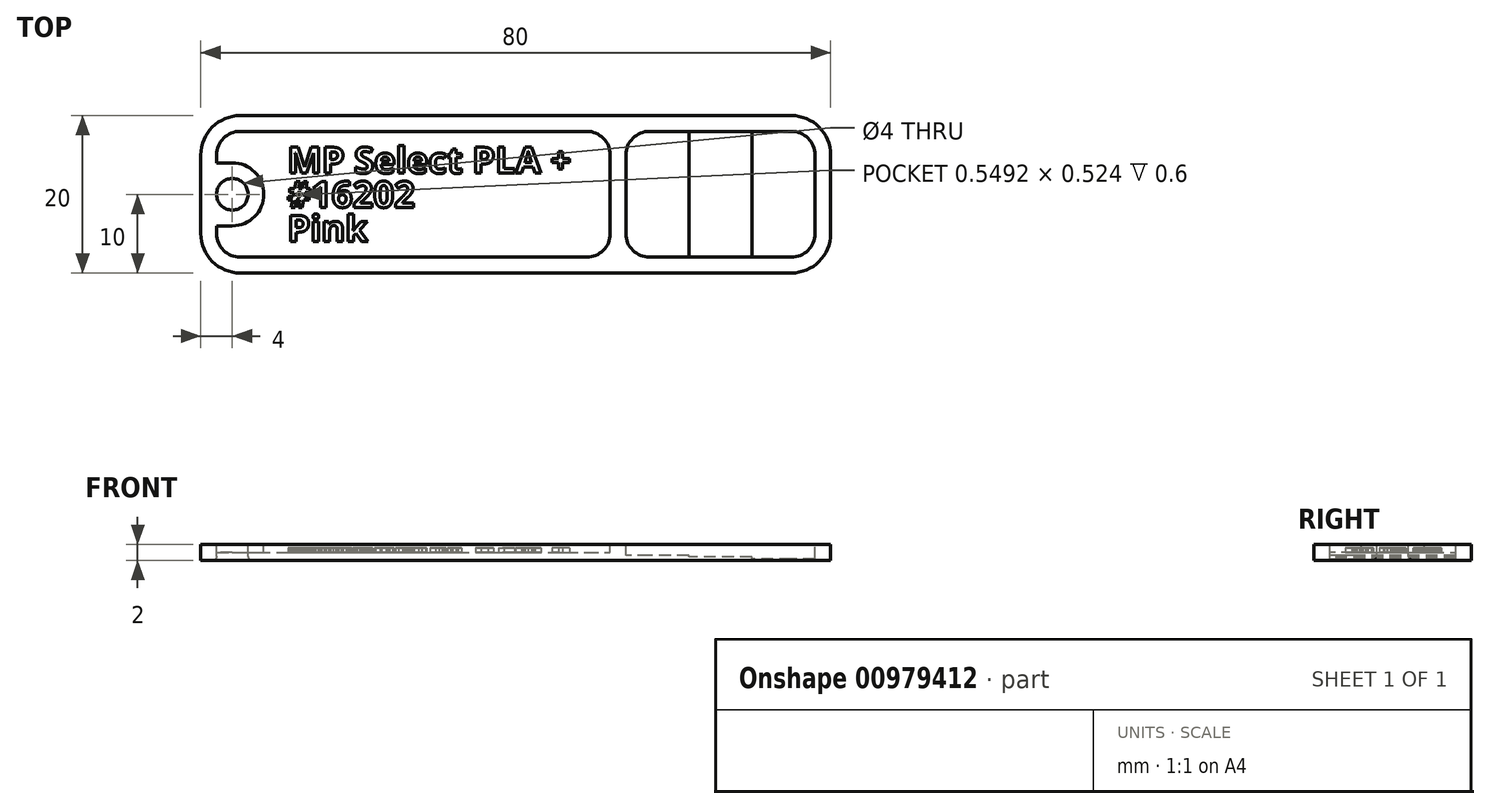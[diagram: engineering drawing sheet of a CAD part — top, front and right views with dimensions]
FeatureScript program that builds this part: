
annotation { "Feature Type Name" : "Feature", "Feature Type Description" : "" }
export const myFeature = defineFeature(function(context is Context, id is Id, definition is map)
    precondition{}
    {
        {
            var Q0;
            Q0=qCreatedBy(makeId("Top.planeOp"),FACE);
            var sketch = newSketch(context, id + "F0", { "sketchPlane" : qUnion([Q0])});
            skLineSegment(sketch, "E0.bottom", {"start": v(35, 10) * mm, "end": v(-35, 10) * mm});
            skLineSegment(sketch, "E0.top", {"start": v(35, -10) * mm, "end": v(-35, -10) * mm});
            skLineSegment(sketch, "E0.left", {"start": v(40, 5) * mm, "end": v(40, -5) * mm});
            skLineSegment(sketch, "E0.right", {"start": v(-40, 5) * mm, "end": v(-40, -5) * mm});
            skPoint(sketch, "E0.middle", {"position": v(0, 0) * mm});
            skPoint(sketch, "E1.visualSharp", {"position": v(-40, 10) * mm});
            skArc(sketch, "E1.filletArc", {"start": v(-35, 10) * mm, "mid": v(-38.54, 8.54) * mm, "end": v(-40, 5) * mm});
            skPoint(sketch, "E2.visualSharp", {"position": v(40, 10) * mm});
            skArc(sketch, "E2.filletArc", {"start": v(40, 5) * mm, "mid": v(38.54, 8.54) * mm, "end": v(35, 10) * mm});
            skPoint(sketch, "E3.visualSharp", {"position": v(40, -10) * mm});
            skArc(sketch, "E3.filletArc", {"start": v(35, -10) * mm, "mid": v(38.54, -8.54) * mm, "end": v(40, -5) * mm});
            skPoint(sketch, "E4.visualSharp", {"position": v(-40, -10) * mm});
            skArc(sketch, "E4.filletArc", {"start": v(-40, -5) * mm, "mid": v(-38.54, -8.54) * mm, "end": v(-35, -10) * mm});
            skSolve(sketch);
        }
        {
            var Q0;
            Q0=qSketchRegion(id+"F0",true);
            extrude(context, id + "F1", {"entities" : qUnion([Q0]), "offsetDistance" : 25 * mm, "depth" : 2 * mm});
        }
        {
            var Q0;
            Q0=makeQuery(id+"F1.opExtrude","CAP_FACE",FACE,{"disambiguationData":[OSD([sQuery(id+"F0.wireOp",EDGE,"E0.bottom"),sQuery(id+"F0.wireOp",EDGE,"E0.top"),sQuery(id+"F0.wireOp",EDGE,"E0.left"),sQuery(id+"F0.wireOp",EDGE,"E0.right"),sQuery(id+"F0.wireOp",EDGE,"E1.filletArc"),sQuery(id+"F0.wireOp",EDGE,"E2.filletArc"),sQuery(id+"F0.wireOp",EDGE,"E3.filletArc"),sQuery(id+"F0.wireOp",EDGE,"E4.filletArc")])],"isStart":false});
            var sketch = newSketch(context, id + "F2", { "sketchPlane" : qUnion([Q0])});
            skLineSegment(sketch, "E5.0", {"start": v(38, -5) * mm, "end": v(38, 5) * mm});
            skArc(sketch, "E5.1", {"start": v(35, -8) * mm, "mid": v(37.12, -7.12) * mm, "end": v(38, -5) * mm});
            skArc(sketch, "E5.2", {"start": v(38, 5) * mm, "mid": v(37.12, 7.12) * mm, "end": v(35, 8) * mm});
            skLineSegment(sketch, "E5.3", {"start": v(-35, -8) * mm, "end": v(9, -8) * mm});
            skLineSegment(sketch, "E5.4", {"start": v(35, 8) * mm, "end": v(17, 8) * mm});
            skArc(sketch, "E5.5", {"start": v(-35, 8) * mm, "mid": v(-37.12, 7.12) * mm, "end": v(-38, 5) * mm});
            skArc(sketch, "E5.7", {"start": v(-38, -5) * mm, "mid": v(-37.12, -7.12) * mm, "end": v(-35, -8) * mm});
            skCircle(sketch, "E6", {"center": v(-36, 0) * mm, "radius": 2 * mm, "construction": true});
            skArc(sketch, "E7.0", {"start": v(-36, -4) * mm, "mid": v(-32, 0) * mm, "end": v(-36, 4) * mm});
            skLineSegment(sketch, "E8", {"start": v(-38, -5) * mm, "end": v(-38, -4) * mm});
            skLineSegment(sketch, "E9", {"start": v(-36, 4) * mm, "end": v(-38, 4) * mm});
            skLineSegment(sketch, "E10", {"start": v(-36, -4) * mm, "end": v(-38, -4) * mm});
            skLineSegment(sketch, "E11.trimOffspring", {"start": v(-38, 4) * mm, "end": v(-38, 5) * mm});
            skArc(sketch, "E12", {"start": v(17, 8) * mm, "mid": v(14.88, 7.12) * mm, "end": v(14, 5) * mm});
            skArc(sketch, "E13", {"start": v(14, -5) * mm, "mid": v(14.88, -7.12) * mm, "end": v(17, -8) * mm});
            skLineSegment(sketch, "E14", {"start": v(14, -5) * mm, "end": v(14, 5) * mm});
            skArc(sketch, "E15", {"start": v(12, 5) * mm, "mid": v(11.12, 7.12) * mm, "end": v(9, 8) * mm});
            skArc(sketch, "E16", {"start": v(12, -5) * mm, "mid": v(11.12, -7.12) * mm, "end": v(9, -8) * mm});
            skLineSegment(sketch, "E17", {"start": v(12, -5) * mm, "end": v(12, 5) * mm});
            skLineSegment(sketch, "E18.trimOffspring", {"start": v(9, 8) * mm, "end": v(-35, 8) * mm});
            skLineSegment(sketch, "E19.trimOffspring", {"start": v(17, -8) * mm, "end": v(35, -8) * mm});
            skSolve(sketch);
        }
        {
            var Q0;
            Q0=qSketchRegion(id+"F2",true);
            extrude(context, id + "F3", {"entities" : qUnion([Q0]), "operationType" : NewBodyOperationType.REMOVE, "oppositeDirection" : true, "offsetDistance" : 25 * mm, "depth" : 1 * mm});
        }
        {
            var Q0;
            Q0=makeQuery(id+"F1.opExtrude","CAP_FACE",FACE,{"disambiguationData":[OSD([sQuery(id+"F0.wireOp",EDGE,"E0.bottom"),sQuery(id+"F0.wireOp",EDGE,"E0.top"),sQuery(id+"F0.wireOp",EDGE,"E0.left"),sQuery(id+"F0.wireOp",EDGE,"E0.right"),sQuery(id+"F0.wireOp",EDGE,"E1.filletArc"),sQuery(id+"F0.wireOp",EDGE,"E2.filletArc"),sQuery(id+"F0.wireOp",EDGE,"E3.filletArc"),sQuery(id+"F0.wireOp",EDGE,"E4.filletArc")])],"isStart":false});
            var sketch = newSketch(context, id + "F4", { "sketchPlane" : qUnion([Q0])});
            skCircle(sketch, "E20.0", {"center": v(-36, 0) * mm, "radius": 2 * mm});
            skSolve(sketch);
        }
        {
            var Q0;
            Q0=qSketchRegion(id+"F4",true);
            extrude(context, id + "F5", {"entities" : qUnion([Q0]), "operationType" : NewBodyOperationType.REMOVE, "endBound" : BoundingType.THROUGH_ALL, "oppositeDirection" : true, "depth" : 25 * mm});
        }
        {
            var Q0;
            Q0=makeQuery(id+"F5.boolean.opBoolean","COPY",EDGE,{"derivedFrom":makeQuery(id+"F5.opExtrude","CAP_EDGE",EDGE,{"disambiguationData":[OSD([sQuery(id+"F4.wireOp",EDGE,"E20.0")])],"isStart":true})});
            var Q1;
            Q1=makeQuery(id+"F5.boolean.opBoolean","INTERSECT",EDGE,{"derivedFrom":[makeQuery(id+"F1.opExtrude","CAP_FACE",FACE,{"disambiguationData":[OSD([sQuery(id+"F0.wireOp",EDGE,"E0.bottom"),sQuery(id+"F0.wireOp",EDGE,"E0.top"),sQuery(id+"F0.wireOp",EDGE,"E0.left"),sQuery(id+"F0.wireOp",EDGE,"E0.right"),sQuery(id+"F0.wireOp",EDGE,"E1.filletArc"),sQuery(id+"F0.wireOp",EDGE,"E2.filletArc"),sQuery(id+"F0.wireOp",EDGE,"E3.filletArc"),sQuery(id+"F0.wireOp",EDGE,"E4.filletArc")])],"isStart":true}),makeQuery(id+"F5.opExtrude","SWEPT_FACE",FACE,{"disambiguationData":[OSD([sQuery(id+"F4.wireOp",EDGE,"E20.0")])]})]});
            fillet(context, id + "F6", {"entities" : qUnion([Q0, Q1]), "radius" : .5 * mm, "tangentPropagation" : true, "allowEdgeOverflow" : false});
        }
        {
            var Q0;
            Q0=makeQuery(id+"F3.boolean.opBoolean","COPY",FACE,{"derivedFrom":makeQuery(id+"F3.opExtrude","CAP_FACE",FACE,{"disambiguationData":[OSD([sQuery(id+"F2.wireOp",EDGE,"E5.0"),sQuery(id+"F2.wireOp",EDGE,"E5.1"),sQuery(id+"F2.wireOp",EDGE,"E5.2"),sQuery(id+"F2.wireOp",EDGE,"E5.4"),sQuery(id+"F2.wireOp",EDGE,"E12"),sQuery(id+"F2.wireOp",EDGE,"E13"),sQuery(id+"F2.wireOp",EDGE,"E14"),sQuery(id+"F2.wireOp",EDGE,"E19.trimOffspring")])],"isStart":false})});
            extrude(context, id + "F7", {"entities" : qUnion([Q0]), "operationType" : NewBodyOperationType.REMOVE, "oppositeDirection" : true, "offsetDistance" : 25 * mm, "depth" : 0.4 * mm});
        }
        {
            var Q0;
            Q0=makeQuery(id+"F7.boolean.opBoolean","COPY",FACE,{"derivedFrom":makeQuery(id+"F7.opExtrude","CAP_FACE",FACE,{"disambiguationData":[OSD([sQuery(id+"F2.wireOp",EDGE,"E5.0"),sQuery(id+"F2.wireOp",EDGE,"E5.1"),sQuery(id+"F2.wireOp",EDGE,"E5.2"),sQuery(id+"F2.wireOp",EDGE,"E5.4"),sQuery(id+"F2.wireOp",EDGE,"E12"),sQuery(id+"F2.wireOp",EDGE,"E13"),sQuery(id+"F2.wireOp",EDGE,"E14"),sQuery(id+"F2.wireOp",EDGE,"E19.trimOffspring")])],"isStart":false})});
            var sketch = newSketch(context, id + "F8", { "sketchPlane" : qUnion([Q0])});
            skArc(sketch, "E21.0.0", {"start": v(35, -8) * mm, "mid": v(37.12, -7.12) * mm, "end": v(38, -5) * mm});
            skLineSegment(sketch, "E21.0.1", {"start": v(38, -5) * mm, "end": v(38, 5) * mm});
            skArc(sketch, "E21.0.2", {"start": v(38, 5) * mm, "mid": v(37.12, 7.12) * mm, "end": v(35, 8) * mm});
            skLineSegment(sketch, "E21.0.3", {"start": v(35, 8) * mm, "end": v(22, 8) * mm});
            skLineSegment(sketch, "E21.0.7", {"start": v(22, -8) * mm, "end": v(35, -8) * mm});
            skLineSegment(sketch, "E22", {"start": v(22, 8) * mm, "end": v(22, -8) * mm});
            skPoint(sketch, "E21.0.4.start.orphan", {"position": v(17, 8) * mm});
            skPoint(sketch, "E21.0.5.start.orphan", {"position": v(14, 5) * mm});
            skPoint(sketch, "E21.0.6.start.orphan", {"position": v(14, -5) * mm});
            skPoint(sketch, "E23.orphan", {"position": v(17, -8) * mm});
            skSolve(sketch);
        }
        {
            var Q0;
            Q0=qSketchRegion(id+"F8",true);
            extrude(context, id + "F9", {"entities" : qUnion([Q0]), "operationType" : NewBodyOperationType.REMOVE, "oppositeDirection" : true, "offsetDistance" : 25 * mm, "depth" : 0.2 * mm});
        }
        {
            var Q0;
            Q0=makeQuery(id+"F9.boolean.opBoolean","COPY",FACE,{"derivedFrom":makeQuery(id+"F9.opExtrude","CAP_FACE",FACE,{"disambiguationData":[OSD([sQuery(id+"F8.wireOp",EDGE,"E21.0.0"),sQuery(id+"F8.wireOp",EDGE,"E21.0.1"),sQuery(id+"F8.wireOp",EDGE,"E21.0.2"),sQuery(id+"F8.wireOp",EDGE,"E21.0.3"),sQuery(id+"F8.wireOp",EDGE,"E21.0.7"),sQuery(id+"F8.wireOp",EDGE,"E22")])],"isStart":false})});
            var sketch = newSketch(context, id + "F10", { "sketchPlane" : qUnion([Q0])});
            skLineSegment(sketch, "E24.0.0", {"start": v(35, 8) * mm, "end": v(30, 8) * mm});
            skLineSegment(sketch, "E24.0.2", {"start": v(30, -8) * mm, "end": v(35, -8) * mm});
            skArc(sketch, "E24.0.3", {"start": v(35, -8) * mm, "mid": v(37.12, -7.12) * mm, "end": v(38, -5) * mm});
            skLineSegment(sketch, "E24.0.4", {"start": v(38, -5) * mm, "end": v(38, 5) * mm});
            skArc(sketch, "E24.0.5", {"start": v(38, 5) * mm, "mid": v(37.12, 7.12) * mm, "end": v(35, 8) * mm});
            skLineSegment(sketch, "E25", {"start": v(30, 8) * mm, "end": v(30, -8) * mm});
            skPoint(sketch, "E24.0.1.end.orphan", {"position": v(22, -8) * mm});
            skPoint(sketch, "E26.orphan", {"position": v(22, 8) * mm});
            skSolve(sketch);
        }
        {
            var Q0;
            Q0=makeQuery(id+"F10.imprint","IMPRINT",FACE,{"disambiguationData":[TD([[makeQuery(id+"F10.imprint","IMPRINT",EDGE,{"derivedFrom":sQuery(id+"F10.wireOp",EDGE,"E24.0.0")}),1.0]])]});
            extrude(context, id + "F11", {"entities" : qUnion([Q0]), "operationType" : NewBodyOperationType.REMOVE, "oppositeDirection" : true, "offsetDistance" : 25 * mm, "depth" : 0.2 * mm});
        }
        {
            var Q0;
            Q0=makeQuery(id+"F3.boolean.opBoolean","COPY",FACE,{"derivedFrom":makeQuery(id+"F3.opExtrude","CAP_FACE",FACE,{"disambiguationData":[OSD([sQuery(id+"F2.wireOp",EDGE,"E5.3"),sQuery(id+"F2.wireOp",EDGE,"E5.5"),sQuery(id+"F2.wireOp",EDGE,"E5.7"),sQuery(id+"F2.wireOp",EDGE,"E7.0"),sQuery(id+"F2.wireOp",EDGE,"E8"),sQuery(id+"F2.wireOp",EDGE,"E9"),sQuery(id+"F2.wireOp",EDGE,"E10"),sQuery(id+"F2.wireOp",EDGE,"E11.trimOffspring"),sQuery(id+"F2.wireOp",EDGE,"E15"),sQuery(id+"F2.wireOp",EDGE,"E16"),sQuery(id+"F2.wireOp",EDGE,"E17"),sQuery(id+"F2.wireOp",EDGE,"E18.trimOffspring")])],"isStart":false})});
            var sketch = newSketch(context, id + "F12", { "sketchPlane" : qUnion([Q0])});
            skText(sketch, "E27", { "text": "MP Select PLA +", "fontName": "OpenSans-Bold.ttf"});
            skText(sketch, "E28", { "text": "#16202", "fontName": "OpenSans-Bold.ttf"});
            skText(sketch, "E29", { "text": "Pink", "fontName": "OpenSans-Bold.ttf"});
            skLineSegment(sketch, "E30", {"start": v(-27.83, 1.67) * mm, "end": v(-27.83, 2.67) * mm, "construction": true});
            skLineSegment(sketch, "E31", {"start": v(-26.66, -2.67) * mm, "end": v(-26.66, -1.67) * mm, "construction": true});
            skLineSegment(sketch, "E32.bottom", {"start": v(-31, 7) * mm, "end": v(10, 7) * mm, "construction": true});
            skLineSegment(sketch, "E32.top", {"start": v(-31, -7) * mm, "end": v(10, -7) * mm, "construction": true});
            skLineSegment(sketch, "E32.left", {"start": v(-31, 7) * mm, "end": v(-31, -7) * mm, "construction": true});
            skLineSegment(sketch, "E32.right", {"start": v(10, 7) * mm, "end": v(10, -7) * mm, "construction": true});
            skLineSegment(sketch, "E33", {"start": v(-13.47, 7) * mm, "end": v(-13.47, 8) * mm, "construction": true});
            skLineSegment(sketch, "E34", {"start": v(-13.67, -7) * mm, "end": v(-13.67, -8) * mm, "construction": true});
            skLineSegment(sketch, "E35", {"start": v(-32, 0) * mm, "end": v(-31, 0) * mm, "construction": true});
            skPoint(sketch, "E35.startSnap0", {"position": v(-31, 0) * mm});
            skLineSegment(sketch, "E36", {"start": v(-29, 4.33) * mm, "end": v(-31, 4.33) * mm, "construction": true});
            skLineSegment(sketch, "E37", {"start": v(10, 1.23) * mm, "end": v(12, 1.23) * mm, "construction": true});
            skLineSegment(sketch, "E38", {"start": v(-29, -0.54) * mm, "end": v(-31, -0.54) * mm, "construction": true});
            skLineSegment(sketch, "E39", {"start": v(-29, -4.33) * mm, "end": v(-31, -4.33) * mm, "construction": true});
            skLineSegment(sketch, "E40", {"start": v(-25.76, 6) * mm, "end": v(-25.76, 7) * mm, "construction": true});
            skLineSegment(sketch, "E41", {"start": v(-26.93, -6) * mm, "end": v(-26.93, -7) * mm, "construction": true});
            const initialGuessF12  = {"E27": [-0.029, 0.00267, 1, 0, 0.00333], "E28": [-0.029, -0.00167, 1, 0, 0.00333], "E29": [-0.029, -0.006, 1, 0, 0.00333]};
            skSetInitialGuess(sketch, initialGuessF12);
            skSolve(sketch);
        }
        {
            var Q0;
            Q0=qSketchRegion(id+"F12",true);
            extrude(context, id + "F13", {"entities" : qUnion([Q0]), "operationType" : NewBodyOperationType.ADD, "depth" : 0.6 * mm, "offsetDistance" : 25 * mm});
        }
    });
